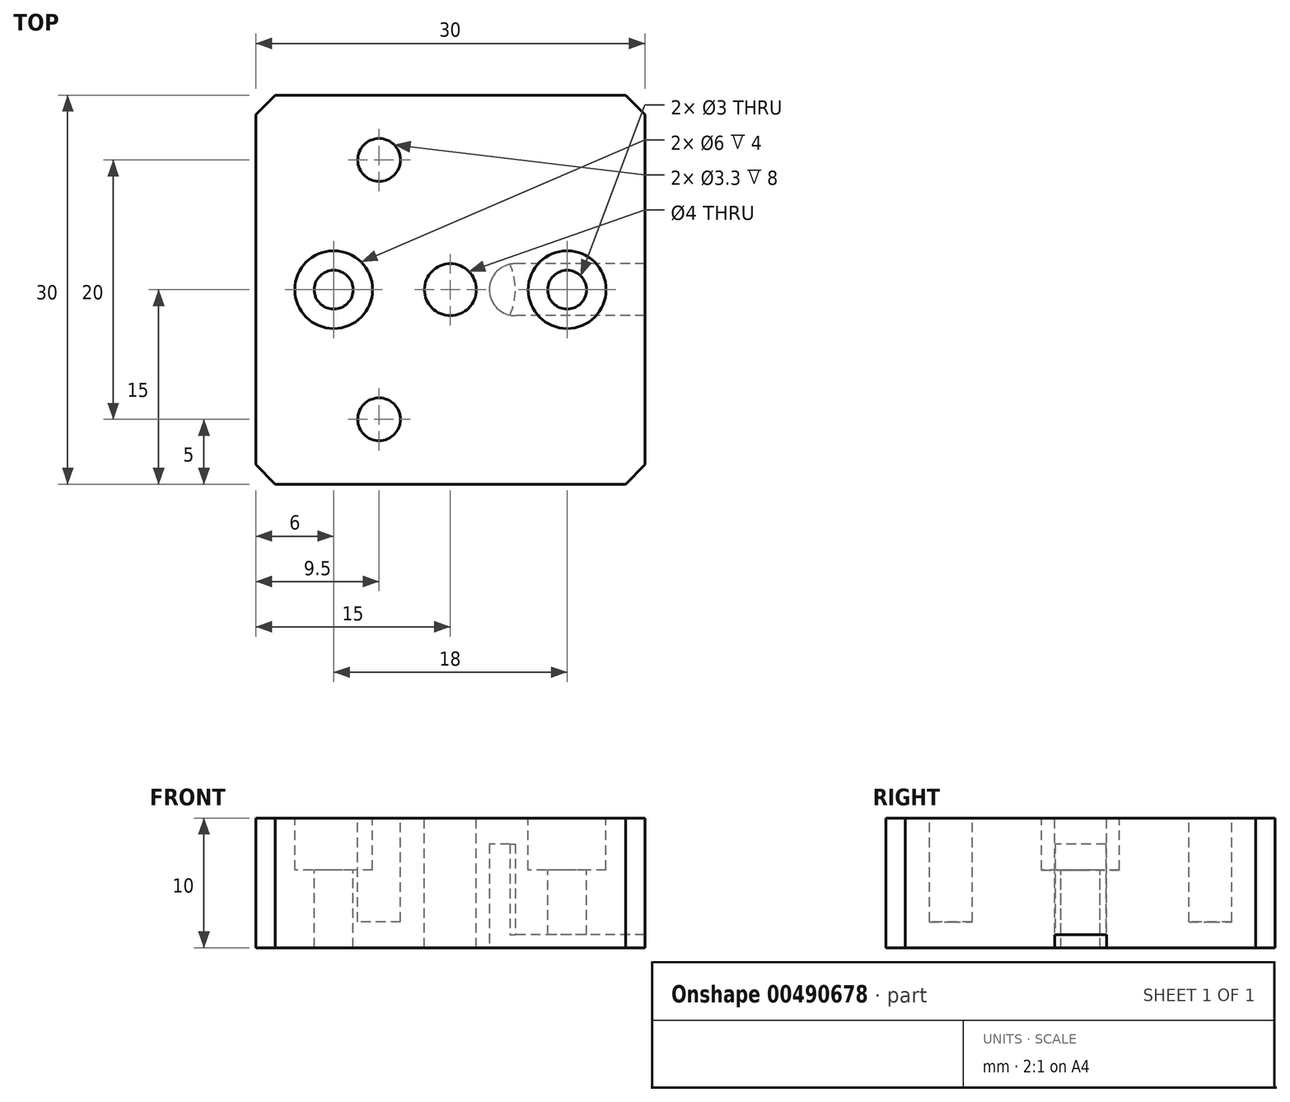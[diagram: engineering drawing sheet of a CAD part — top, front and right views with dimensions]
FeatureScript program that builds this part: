
annotation { "Feature Type Name" : "Feature", "Feature Type Description" : "" }
export const myFeature = defineFeature(function(context is Context, id is Id, definition is map)
    precondition{}
    {
        {
            var Q0;
            Q0=qCreatedBy(makeId("Top.planeOp"),FACE);
            var sketch = newSketch(context, id + "F0", { "sketchPlane" : qUnion([Q0])});
            skLineSegment(sketch, "E0.bottom", {"start": v(0, 0) * mm, "end": v(30, 0) * mm});
            skLineSegment(sketch, "E0.top", {"start": v(0, -30) * mm, "end": v(30, -30) * mm});
            skLineSegment(sketch, "E0.left", {"start": v(0, 0) * mm, "end": v(0, -30) * mm});
            skLineSegment(sketch, "E0.right", {"start": v(30, 0) * mm, "end": v(30, -30) * mm});
            skLineSegment(sketch, "E1", {"start": v(0, -15) * mm, "end": v(30, -15) * mm, "construction": true});
            skCircle(sketch, "E2", {"center": v(15, -15) * mm, "radius": 2 * mm});
            skLineSegment(sketch, "E3", {"start": v(0, -5) * mm, "end": v(9.5, -5) * mm, "construction": true});
            skLineSegment(sketch, "E4", {"start": v(9.5, -5) * mm, "end": v(9.5, 0) * mm, "construction": true});
            skCircle(sketch, "E5", {"center": v(9.5, -5) * mm, "radius": 1.65 * mm});
            skCircle(sketch, "E6.0.1.0", {"center": v(9.5, -25) * mm, "radius": 1.65 * mm});
            skLineSegment(sketch, "E6.direction2", {"start": v(9.5, -5) * mm, "end": v(9.5, -25) * mm, "construction": true});
            skLineSegment(sketch, "E7", {"start": v(15, -30) * mm, "end": v(15, 0) * mm, "construction": true});
            skCircle(sketch, "E8", {"center": v(15, -6) * mm, "radius": 1.5 * mm});
            skCircle(sketch, "E9", {"center": v(15, -24) * mm, "radius": 1.5 * mm});
            skCircle(sketch, "E10", {"center": v(15, -6) * mm, "radius": 3 * mm});
            skCircle(sketch, "E11", {"center": v(15, -24) * mm, "radius": 3 * mm});
            skCircle(sketch, "E12", {"center": v(6, -15) * mm, "radius": 1.5 * mm});
            skCircle(sketch, "E13", {"center": v(6, -15) * mm, "radius": 3 * mm});
            skCircle(sketch, "E14", {"center": v(24, -15) * mm, "radius": 3 * mm});
            skCircle(sketch, "E15", {"center": v(24, -15) * mm, "radius": 1.5 * mm});
            skSolve(sketch);
        }
        {
            var Q0;
            Q0=makeQuery(id+"F0.imprint","IMPRINT",FACE,{"disambiguationData":[TD([[makeQuery(id+"F0.imprint","IMPRINT",EDGE,{"derivedFrom":sQuery(id+"F0.wireOp",EDGE,"E0.bottom")}),-1.0]])]});
            var Q1;
            Q1=makeQuery(id+"F0.imprint","IMPRINT",FACE,{"disambiguationData":[TD([[makeQuery(id+"F0.imprint","IMPRINT",EDGE,{"derivedFrom":sQuery(id+"F0.wireOp",EDGE,"E2")}),1.0]])]});
            var Q2;
            Q2=makeQuery(id+"F0.imprint","IMPRINT",FACE,{"disambiguationData":[TD([[makeQuery(id+"F0.imprint","IMPRINT",EDGE,{"derivedFrom":sQuery(id+"F0.wireOp",EDGE,"E8")}),-1.0]])]});
            var Q3;
            Q3=makeQuery(id+"F0.imprint","IMPRINT",FACE,{"disambiguationData":[TD([[makeQuery(id+"F0.imprint","IMPRINT",EDGE,{"derivedFrom":sQuery(id+"F0.wireOp",EDGE,"E9")}),-1.0]])]});
            var Q4;
            Q4=makeQuery(id+"F0.imprint","IMPRINT",FACE,{"disambiguationData":[TD([[makeQuery(id+"F0.imprint","IMPRINT",EDGE,{"derivedFrom":sQuery(id+"F0.wireOp",EDGE,"E5")}),1.0]])]});
            var Q5;
            Q5=makeQuery(id+"F0.imprint","IMPRINT",FACE,{"disambiguationData":[TD([[makeQuery(id+"F0.imprint","IMPRINT",EDGE,{"derivedFrom":sQuery(id+"F0.wireOp",EDGE,"E6.0.1.0")}),1.0]])]});
            var Q6;
            Q6=makeQuery(id+"F0.imprint","IMPRINT",FACE,{"disambiguationData":[TD([[makeQuery(id+"F0.imprint","IMPRINT",EDGE,{"derivedFrom":sQuery(id+"F0.wireOp",EDGE,"E14")}),1.0]])]});
            var Q7;
            Q7=makeQuery(id+"F0.imprint","IMPRINT",FACE,{"disambiguationData":[TD([[makeQuery(id+"F0.imprint","IMPRINT",EDGE,{"derivedFrom":sQuery(id+"F0.wireOp",EDGE,"E12")}),-1.0]])]});
            var Q8;
            Q8=makeQuery(id+"F0.imprint","IMPRINT",FACE,{"disambiguationData":[TD([[makeQuery(id+"F0.imprint","IMPRINT",EDGE,{"derivedFrom":sQuery(id+"F0.wireOp",EDGE,"E9")}),1.0]])]});
            var Q9;
            Q9=makeQuery(id+"F0.imprint","IMPRINT",FACE,{"disambiguationData":[TD([[makeQuery(id+"F0.imprint","IMPRINT",EDGE,{"derivedFrom":sQuery(id+"F0.wireOp",EDGE,"E8")}),1.0]])]});
            extrude(context, id + "F1", {"entities" : qUnion([Q0, Q1, Q2, Q3, Q4, Q5, Q6, Q7, Q8, Q9]), "oppositeDirection" : true, "depth" : 10 * mm, "offsetDistance" : 25 * mm});
        }
        {
            var Q0;
            Q0=makeQuery(id+"F0.imprint","IMPRINT",FACE,{"disambiguationData":[TD([[makeQuery(id+"F0.imprint","IMPRINT",EDGE,{"derivedFrom":sQuery(id+"F0.wireOp",EDGE,"CrWIfdQ6-x99r-vkrS-wa22-O8fHmD59tpvO")}),1.0]])]});
            var Q1;
            Q1=makeQuery(id+"F0.imprint","IMPRINT",FACE,{"disambiguationData":[TD([[makeQuery(id+"F0.imprint","IMPRINT",EDGE,{"derivedFrom":sQuery(id+"F0.wireOp",EDGE,"E2")}),1.0]])]});
            extrude(context, id + "F2", {"entities" : qUnion([Q0, Q1]), "operationType" : NewBodyOperationType.REMOVE, "oppositeDirection" : true, "depth" : 12 * mm, "offsetDistance" : 25 * mm});
        }
        {
            var Q0;
            Q0=makeQuery(id+"F1.opExtrude","SWEPT_EDGE",EDGE,{"disambiguationData":[OSD([sQuery(id+"F0.wireOp",EDGE,"E0.top"),sQuery(id+"F0.wireOp",EDGE,"E0.right")])]});
            var Q1;
            Q1=makeQuery(id+"F1.opExtrude","SWEPT_EDGE",EDGE,{"disambiguationData":[OSD([sQuery(id+"F0.wireOp",EDGE,"E0.top"),sQuery(id+"F0.wireOp",EDGE,"E0.left")])]});
            var Q2;
            Q2=makeQuery(id+"F1.opExtrude","SWEPT_EDGE",EDGE,{"disambiguationData":[OSD([sQuery(id+"F0.wireOp",EDGE,"E0.bottom"),sQuery(id+"F0.wireOp",EDGE,"E0.left")])]});
            var Q3;
            Q3=makeQuery(id+"F1.opExtrude","SWEPT_EDGE",EDGE,{"disambiguationData":[OSD([sQuery(id+"F0.wireOp",EDGE,"E0.bottom"),sQuery(id+"F0.wireOp",EDGE,"E0.right")])]});
            chamfer(context, id + "F3", {"entities" : qUnion([Q0, Q1, Q2, Q3]), "width" : 1.5 * mm, "tangentPropagation" : true});
        }
        {
            var Q0;
            Q0=makeQuery(id+"F0.imprint","IMPRINT",FACE,{"disambiguationData":[TD([[makeQuery(id+"F0.imprint","IMPRINT",EDGE,{"derivedFrom":sQuery(id+"F0.wireOp",EDGE,"E12")}),-1.0]])]});
            var Q1;
            Q1=makeQuery(id+"F0.imprint","IMPRINT",FACE,{"disambiguationData":[TD([[makeQuery(id+"F0.imprint","IMPRINT",EDGE,{"derivedFrom":sQuery(id+"F0.wireOp",EDGE,"E14")}),1.0]])]});
            extrude(context, id + "F4", {"entities" : qUnion([Q0, Q1]), "operationType" : NewBodyOperationType.REMOVE, "oppositeDirection" : true, "depth" : 4 * mm, "offsetDistance" : 25 * mm});
        }
        {
            var Q0;
            Q0=makeQuery(id+"F0.imprint","IMPRINT",FACE,{"disambiguationData":[TD([[makeQuery(id+"F0.imprint","IMPRINT",EDGE,{"derivedFrom":sQuery(id+"F0.wireOp",EDGE,"E5")}),1.0]])]});
            var Q1;
            Q1=makeQuery(id+"F0.imprint","IMPRINT",FACE,{"disambiguationData":[TD([[makeQuery(id+"F0.imprint","IMPRINT",EDGE,{"derivedFrom":sQuery(id+"F0.wireOp",EDGE,"E6.0.1.0")}),1.0]])]});
            extrude(context, id + "F5", {"entities" : qUnion([Q0, Q1]), "operationType" : NewBodyOperationType.REMOVE, "oppositeDirection" : true, "depth" : 8 * mm, "offsetDistance" : 25 * mm});
        }
        {
            var Q0;
            Q0=makeQuery(id+"F1.opExtrude","CAP_FACE",FACE,{"disambiguationData":[OSD([sQuery(id+"F0.wireOp",EDGE,"E0.bottom"),sQuery(id+"F0.wireOp",EDGE,"E0.top"),sQuery(id+"F0.wireOp",EDGE,"E0.left"),sQuery(id+"F0.wireOp",EDGE,"E0.right"),sQuery(id+"F0.wireOp",EDGE,"E8"),sQuery(id+"F0.wireOp",EDGE,"E9")])],"isStart":false});
            var sketch = newSketch(context, id + "F6", { "sketchPlane" : qUnion([Q0])});
            skCircle(sketch, "E16", {"center": v(15, 15) * mm, "radius": 5 * mm});
            skLineSegment(sketch, "E17", {"start": v(30, 15) * mm, "end": v(20, 15) * mm, "construction": true});
            skArc(sketch, "E18.0.startCap", {"start": v(30, 17) * mm, "mid": v(32, 15) * mm, "end": v(30, 13) * mm});
            skArc(sketch, "E18.0.endCap", {"start": v(20, 13) * mm, "mid": v(18, 15) * mm, "end": v(20, 17) * mm});
            skLineSegment(sketch, "E18.0.left", {"start": v(30, 13) * mm, "end": v(20, 13) * mm});
            skLineSegment(sketch, "E18.0.right", {"start": v(30, 17) * mm, "end": v(20, 17) * mm});
            skLineSegment(sketch, "E19", {"start": v(3.5, 0) * mm, "end": v(3.5, 3.5) * mm, "construction": true});
            skLineSegment(sketch, "E20", {"start": v(3.5, 3.5) * mm, "end": v(0, 3.5) * mm, "construction": true});
            skCircle(sketch, "E21", {"center": v(3.5, 3.5) * mm, "radius": 1.25 * mm});
            skCircle(sketch, "E22", {"center": v(3.5, 3.5) * mm, "radius": 2.5 * mm});
            skCircle(sketch, "E23.0.1.0", {"center": v(3.5, 26.5) * mm, "radius": 1.25 * mm});
            skCircle(sketch, "E23.0.1.1", {"center": v(3.5, 26.5) * mm, "radius": 2.5 * mm});
            skCircle(sketch, "E23.1.0.0", {"center": v(26.5, 3.5) * mm, "radius": 1.25 * mm});
            skCircle(sketch, "E23.1.0.1", {"center": v(26.5, 3.5) * mm, "radius": 2.5 * mm});
            skCircle(sketch, "E23.1.1.0", {"center": v(26.5, 26.5) * mm, "radius": 1.25 * mm});
            skCircle(sketch, "E23.1.1.1", {"center": v(26.5, 26.5) * mm, "radius": 2.5 * mm});
            skLineSegment(sketch, "E23.direction1", {"start": v(3.5, 3.5) * mm, "end": v(26.5, 3.5) * mm, "construction": true});
            skLineSegment(sketch, "E23.direction2", {"start": v(3.5, 3.5) * mm, "end": v(3.5, 26.5) * mm, "construction": true});
            skSolve(sketch);
        }
        {
            var Q0;
            Q0=makeQuery(id+"F6.imprint","IMPRINT",FACE,{"disambiguationData":[TD([[makeQuery(id+"F6.imprint","IMPRINT",EDGE,{"derivedFrom":sQuery(id+"F6.wireOp",EDGE,"E16")}),1.0]])]});
            var Q1;
            {var subQ0=sQuery(id+"F6.wireOp",EDGE,"E18.0.endCap");var subQ1=sQuery(id+"F6.wireOp",EDGE,"E16");var subQ2=makeQuery(id+"F6.imprint","INTERSECT",VERTEX,{"disambiguationData":[OD(0.0)],"derivedFrom":[subQ1,subQ0]});Q1=makeQuery(id+"F6.imprint","IMPRINT",FACE,{"disambiguationData":[TD([[makeQuery(id+"F6.imprint","IMPRINT",EDGE,{"disambiguationData":[TD([[subQ2,1.0]])],"derivedFrom":subQ1}),1.0]])]});}
            extrude(context, id + "F7", {"entities" : qUnion([Q0, Q1]), "operationType" : NewBodyOperationType.REMOVE, "oppositeDirection" : true, "depth" : 8 * mm, "offsetDistance" : 25 * mm});
        }
        {
            var Q0;
            {var subQ4=sQuery(id+"F6.wireOp",EDGE,"E18.0.left");Q0=makeQuery(id+"F6.imprint","IMPRINT",FACE,{"disambiguationData":[TD([[makeQuery(id+"F6.imprint","IMPRINT",EDGE,{"derivedFrom":subQ4}),-1.0]])]});}
            extrude(context, id + "F8", {"entities" : qUnion([Q0]), "operationType" : NewBodyOperationType.REMOVE, "oppositeDirection" : true, "depth" : 1 * mm, "offsetDistance" : 25 * mm});
        }
    });
